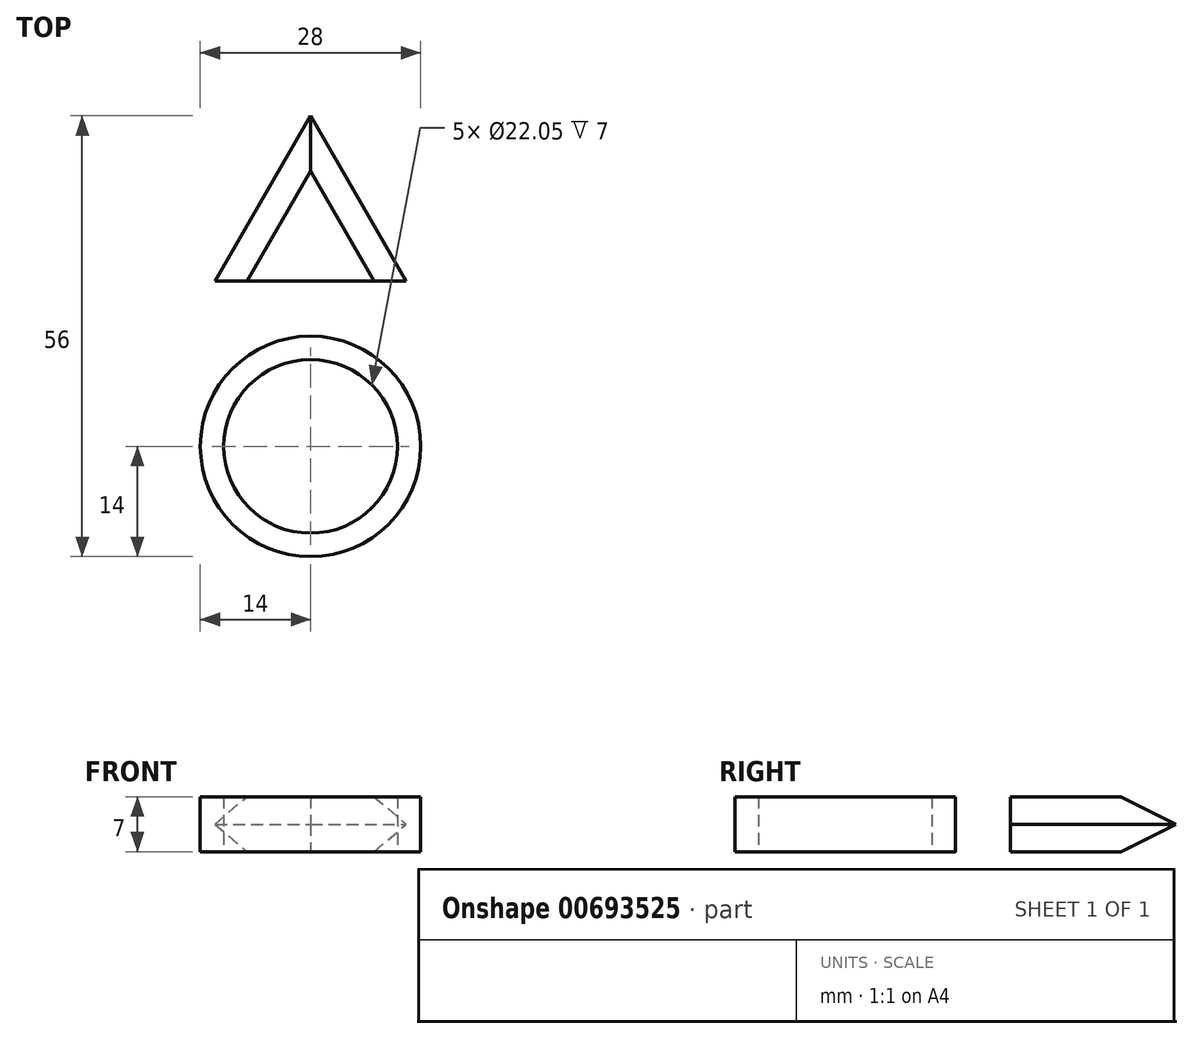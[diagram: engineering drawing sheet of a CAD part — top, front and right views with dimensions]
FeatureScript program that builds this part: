
annotation { "Feature Type Name" : "Feature", "Feature Type Description" : "" }
export const myFeature = defineFeature(function(context is Context, id is Id, definition is map)
    precondition{}
    {
        {
            var Q0;
            Q0=qCreatedBy(makeId("Top.planeOp"),FACE);
            var sketch = newSketch(context, id + "F0", { "sketchPlane" : qUnion([Q0])});
            skCircle(sketch, "E0.cCircle", {"center": v(0, 18.9) * mm, "radius": 14 * mm, "construction": true});
            skLineSegment(sketch, "E0.0", {"start": v(12.12, 11.9) * mm, "end": v(-12.12, 11.9) * mm});
            skLineSegment(sketch, "E0.1", {"start": v(-12.12, 11.9) * mm, "end": v(0, 32.9) * mm});
            skLineSegment(sketch, "E0.2", {"start": v(0, 32.9) * mm, "end": v(12.12, 11.9) * mm});
            skCircle(sketch, "E1.cCircle", {"center": v(0, 4.9) * mm, "radius": 14 * mm, "construction": true});
            skPoint(sketch, "E1.cCircle.centerSnap0", {"position": v(0, 11.9) * mm});
            skLineSegment(sketch, "E1.0", {"start": v(0, -9.1) * mm, "end": v(-12.12, 11.9) * mm});
            skLineSegment(sketch, "E1.1", {"start": v(-12.12, 11.9) * mm, "end": v(12.12, 11.9) * mm});
            skLineSegment(sketch, "E1.2", {"start": v(12.12, 11.9) * mm, "end": v(0, -9.1) * mm});
            skCircle(sketch, "E2", {"center": v(0, -9.1) * mm, "radius": 14 * mm});
            skCircle(sketch, "E3", {"center": v(0, -9.1) * mm, "radius": 11.03 * mm});
            skSolve(sketch);
        }
        {
            var Q0;
            Q0=makeQuery(id+"F0.imprint","IMPRINT",FACE,{"disambiguationData":[TD([[makeQuery(id+"F0.imprint","IMPRINT",EDGE,{"derivedFrom":sQuery(id+"F0.wireOp",EDGE,"E0.1")}),-1.0]])]});
            var Q1;
            {var subQ0=sQuery(id+"F0.wireOp",EDGE,"E1.1");Q1=makeQuery(id+"F0.imprint","IMPRINT",FACE,{"disambiguationData":[TD([[makeQuery(id+"F0.imprint","IMPRINT",EDGE,{"derivedFrom":subQ0}),-1.0]])]});}
            var Q2;
            {var subQ0=sQuery(id+"F0.wireOp",EDGE,"E2");var subQ1=sQuery(id+"F0.wireOp",EDGE,"E1.0");var subQ2=makeQuery(id+"F0.imprint","INTERSECT",VERTEX,{"derivedFrom":[subQ1,subQ0]});Q2=makeQuery(id+"F0.imprint","IMPRINT",FACE,{"disambiguationData":[TD([[makeQuery(id+"F0.imprint","IMPRINT",EDGE,{"disambiguationData":[TD([[subQ2,1.0]])],"derivedFrom":subQ1}),-1.0]])]});}
            var Q3;
            {var subQ0=sQuery(id+"F0.wireOp",EDGE,"E2");var subQ1=sQuery(id+"F0.wireOp",EDGE,"E1.0");var subQ2=makeQuery(id+"F0.imprint","INTERSECT",VERTEX,{"derivedFrom":[subQ1,subQ0]});Q3=makeQuery(id+"F0.imprint","IMPRINT",FACE,{"disambiguationData":[TD([[makeQuery(id+"F0.imprint","IMPRINT",EDGE,{"disambiguationData":[TD([[subQ2,1.0]])],"derivedFrom":subQ1}),1.0]])]});}
            extrude(context, id + "F1", {"entities" : qUnion([Q0, Q1, Q2, Q3]), "depth" : 7 * mm, "offsetDistance" : 25.4 * mm});
        }
        {
            var Q0;
            Q0=makeQuery(id+"F1.opExtrude","SWEPT_BODY",BODY,{"disambiguationData":[OSD([sQuery(id+"F0.wireOp",EDGE,"E0.1"),sQuery(id+"F0.wireOp",EDGE,"E0.2"),sQuery(id+"F0.wireOp",EDGE,"E1.0"),sQuery(id+"F0.wireOp",EDGE,"E1.2"),sQuery(id+"F0.wireOp",EDGE,"E2"),sQuery(id+"F0.wireOp",EDGE,"E3")])]});
            var Q1;
            Q1=makeQuery(id+"F1.opExtrude","SWEPT_FACE",FACE,{"disambiguationData":[OSD([sQuery(id+"F0.wireOp",EDGE,"E2")])]});
            circularPattern(context, id + "F2", {"operationType" : NewBodyOperationType.ADD, "entities" : qUnion([Q0]), "axis" : qUnion([Q1]), "angle" : 360 * degree, "instanceCount" : 5, "equalSpace" : true});
        }
        {
            var Q0;
            Q0=makeQuery(id+"F2.opPattern","COPY",EDGE,{"derivedFrom":makeQuery(id+"F1.opExtrude","CAP_EDGE",EDGE,{"disambiguationData":[OSD([sQuery(id+"F0.wireOp",EDGE,"E0.1")])],"isStart":false}),"instanceName":"3"});
            var Q1;
            Q1=makeQuery(id+"F2.opPattern","COPY",EDGE,{"derivedFrom":makeQuery(id+"F1.opExtrude","CAP_EDGE",EDGE,{"disambiguationData":[OSD([sQuery(id+"F0.wireOp",EDGE,"E0.2")])],"isStart":false}),"instanceName":"3"});
            var Q2;
            Q2=makeQuery(id+"F2.opPattern","COPY",EDGE,{"derivedFrom":makeQuery(id+"F1.opExtrude","CAP_EDGE",EDGE,{"disambiguationData":[OSD([sQuery(id+"F0.wireOp",EDGE,"E1.0")])],"isStart":false}),"instanceName":"4"});
            var Q3;
            Q3=makeQuery(id+"F2.opPattern","COPY",EDGE,{"derivedFrom":makeQuery(id+"F1.opExtrude","CAP_EDGE",EDGE,{"disambiguationData":[OSD([sQuery(id+"F0.wireOp",EDGE,"E1.2")])],"isStart":false}),"instanceName":"3"});
            var Q4;
            Q4=makeQuery(id+"F2.opPattern","COPY",EDGE,{"derivedFrom":makeQuery(id+"F1.opExtrude","CAP_EDGE",EDGE,{"disambiguationData":[OSD([sQuery(id+"F0.wireOp",EDGE,"E0.1")])],"isStart":false}),"instanceName":"4"});
            var Q5;
            Q5=makeQuery(id+"F2.opPattern","COPY",EDGE,{"derivedFrom":makeQuery(id+"F1.opExtrude","CAP_EDGE",EDGE,{"disambiguationData":[OSD([sQuery(id+"F0.wireOp",EDGE,"E0.2")])],"isStart":false}),"instanceName":"4"});
            var Q6;
            Q6=makeQuery(id+"F1.opExtrude","CAP_EDGE",EDGE,{"disambiguationData":[OSD([sQuery(id+"F0.wireOp",EDGE,"E1.0")])],"isStart":false});
            var Q7;
            Q7=makeQuery(id+"F2.opPattern","COPY",EDGE,{"derivedFrom":makeQuery(id+"F1.opExtrude","CAP_EDGE",EDGE,{"disambiguationData":[OSD([sQuery(id+"F0.wireOp",EDGE,"E1.2")])],"isStart":false}),"instanceName":"4"});
            var Q8;
            Q8=makeQuery(id+"F1.opExtrude","CAP_EDGE",EDGE,{"disambiguationData":[OSD([sQuery(id+"F0.wireOp",EDGE,"E0.1")])],"isStart":false});
            var Q9;
            Q9=makeQuery(id+"F1.opExtrude","CAP_EDGE",EDGE,{"disambiguationData":[OSD([sQuery(id+"F0.wireOp",EDGE,"E0.2")])],"isStart":false});
            var Q10;
            Q10=makeQuery(id+"F1.opExtrude","CAP_EDGE",EDGE,{"disambiguationData":[OSD([sQuery(id+"F0.wireOp",EDGE,"E1.2")])],"isStart":false});
            var Q11;
            Q11=makeQuery(id+"F2.opPattern","COPY",EDGE,{"derivedFrom":makeQuery(id+"F1.opExtrude","CAP_EDGE",EDGE,{"disambiguationData":[OSD([sQuery(id+"F0.wireOp",EDGE,"E1.0")])],"isStart":false}),"instanceName":"1"});
            var Q12;
            Q12=makeQuery(id+"F2.opPattern","COPY",EDGE,{"derivedFrom":makeQuery(id+"F1.opExtrude","CAP_EDGE",EDGE,{"disambiguationData":[OSD([sQuery(id+"F0.wireOp",EDGE,"E0.1")])],"isStart":false}),"instanceName":"1"});
            var Q13;
            Q13=makeQuery(id+"F2.opPattern","COPY",EDGE,{"derivedFrom":makeQuery(id+"F1.opExtrude","CAP_EDGE",EDGE,{"disambiguationData":[OSD([sQuery(id+"F0.wireOp",EDGE,"E0.2")])],"isStart":false}),"instanceName":"1"});
            var Q14;
            Q14=makeQuery(id+"F2.opPattern","COPY",EDGE,{"derivedFrom":makeQuery(id+"F1.opExtrude","CAP_EDGE",EDGE,{"disambiguationData":[OSD([sQuery(id+"F0.wireOp",EDGE,"E1.2")])],"isStart":false}),"instanceName":"1"});
            var Q15;
            Q15=makeQuery(id+"F2.opPattern","COPY",EDGE,{"derivedFrom":makeQuery(id+"F1.opExtrude","CAP_EDGE",EDGE,{"disambiguationData":[OSD([sQuery(id+"F0.wireOp",EDGE,"E1.0")])],"isStart":false}),"instanceName":"2"});
            var Q16;
            Q16=makeQuery(id+"F2.opPattern","COPY",EDGE,{"derivedFrom":makeQuery(id+"F1.opExtrude","CAP_EDGE",EDGE,{"disambiguationData":[OSD([sQuery(id+"F0.wireOp",EDGE,"E0.1")])],"isStart":false}),"instanceName":"2"});
            var Q17;
            Q17=makeQuery(id+"F2.opPattern","COPY",EDGE,{"derivedFrom":makeQuery(id+"F1.opExtrude","CAP_EDGE",EDGE,{"disambiguationData":[OSD([sQuery(id+"F0.wireOp",EDGE,"E0.2")])],"isStart":false}),"instanceName":"2"});
            var Q18;
            Q18=makeQuery(id+"F2.opPattern","COPY",EDGE,{"derivedFrom":makeQuery(id+"F1.opExtrude","CAP_EDGE",EDGE,{"disambiguationData":[OSD([sQuery(id+"F0.wireOp",EDGE,"E1.2")])],"isStart":false}),"instanceName":"2"});
            var Q19;
            Q19=makeQuery(id+"F2.opPattern","COPY",EDGE,{"derivedFrom":makeQuery(id+"F1.opExtrude","CAP_EDGE",EDGE,{"disambiguationData":[OSD([sQuery(id+"F0.wireOp",EDGE,"E1.0")])],"isStart":false}),"instanceName":"3"});
            var Q20;
            Q20=makeQuery(id+"F2.opPattern","COPY",EDGE,{"derivedFrom":makeQuery(id+"F1.opExtrude","CAP_EDGE",EDGE,{"disambiguationData":[OSD([sQuery(id+"F0.wireOp",EDGE,"E0.1")])],"isStart":true}),"instanceName":"3"});
            var Q21;
            Q21=makeQuery(id+"F2.opPattern","COPY",EDGE,{"derivedFrom":makeQuery(id+"F1.opExtrude","CAP_EDGE",EDGE,{"disambiguationData":[OSD([sQuery(id+"F0.wireOp",EDGE,"E0.2")])],"isStart":true}),"instanceName":"3"});
            var Q22;
            Q22=makeQuery(id+"F2.opPattern","COPY",EDGE,{"derivedFrom":makeQuery(id+"F1.opExtrude","CAP_EDGE",EDGE,{"disambiguationData":[OSD([sQuery(id+"F0.wireOp",EDGE,"E1.0")])],"isStart":true}),"instanceName":"3"});
            var Q23;
            Q23=makeQuery(id+"F2.opPattern","COPY",EDGE,{"derivedFrom":makeQuery(id+"F1.opExtrude","CAP_EDGE",EDGE,{"disambiguationData":[OSD([sQuery(id+"F0.wireOp",EDGE,"E1.2")])],"isStart":true}),"instanceName":"2"});
            var Q24;
            Q24=makeQuery(id+"F2.opPattern","COPY",EDGE,{"derivedFrom":makeQuery(id+"F1.opExtrude","CAP_EDGE",EDGE,{"disambiguationData":[OSD([sQuery(id+"F0.wireOp",EDGE,"E0.2")])],"isStart":true}),"instanceName":"2"});
            var Q25;
            Q25=makeQuery(id+"F2.opPattern","COPY",EDGE,{"derivedFrom":makeQuery(id+"F1.opExtrude","CAP_EDGE",EDGE,{"disambiguationData":[OSD([sQuery(id+"F0.wireOp",EDGE,"E0.1")])],"isStart":true}),"instanceName":"2"});
            var Q26;
            Q26=makeQuery(id+"F2.opPattern","COPY",EDGE,{"derivedFrom":makeQuery(id+"F1.opExtrude","CAP_EDGE",EDGE,{"disambiguationData":[OSD([sQuery(id+"F0.wireOp",EDGE,"E1.0")])],"isStart":true}),"instanceName":"2"});
            var Q27;
            Q27=makeQuery(id+"F2.opPattern","COPY",EDGE,{"derivedFrom":makeQuery(id+"F1.opExtrude","CAP_EDGE",EDGE,{"disambiguationData":[OSD([sQuery(id+"F0.wireOp",EDGE,"E1.2")])],"isStart":true}),"instanceName":"1"});
            var Q28;
            Q28=makeQuery(id+"F2.opPattern","COPY",EDGE,{"derivedFrom":makeQuery(id+"F1.opExtrude","CAP_EDGE",EDGE,{"disambiguationData":[OSD([sQuery(id+"F0.wireOp",EDGE,"E0.2")])],"isStart":true}),"instanceName":"1"});
            var Q29;
            Q29=makeQuery(id+"F2.opPattern","COPY",EDGE,{"derivedFrom":makeQuery(id+"F1.opExtrude","CAP_EDGE",EDGE,{"disambiguationData":[OSD([sQuery(id+"F0.wireOp",EDGE,"E0.1")])],"isStart":true}),"instanceName":"1"});
            var Q30;
            Q30=makeQuery(id+"F2.opPattern","COPY",EDGE,{"derivedFrom":makeQuery(id+"F1.opExtrude","CAP_EDGE",EDGE,{"disambiguationData":[OSD([sQuery(id+"F0.wireOp",EDGE,"E1.0")])],"isStart":true}),"instanceName":"1"});
            var Q31;
            Q31=makeQuery(id+"F1.opExtrude","CAP_EDGE",EDGE,{"disambiguationData":[OSD([sQuery(id+"F0.wireOp",EDGE,"E1.2")])],"isStart":true});
            var Q32;
            Q32=makeQuery(id+"F1.opExtrude","CAP_EDGE",EDGE,{"disambiguationData":[OSD([sQuery(id+"F0.wireOp",EDGE,"E0.2")])],"isStart":true});
            var Q33;
            Q33=makeQuery(id+"F1.opExtrude","CAP_EDGE",EDGE,{"disambiguationData":[OSD([sQuery(id+"F0.wireOp",EDGE,"E0.1")])],"isStart":true});
            var Q34;
            Q34=makeQuery(id+"F1.opExtrude","CAP_EDGE",EDGE,{"disambiguationData":[OSD([sQuery(id+"F0.wireOp",EDGE,"E1.0")])],"isStart":true});
            var Q35;
            Q35=makeQuery(id+"F2.opPattern","COPY",EDGE,{"derivedFrom":makeQuery(id+"F1.opExtrude","CAP_EDGE",EDGE,{"disambiguationData":[OSD([sQuery(id+"F0.wireOp",EDGE,"E1.2")])],"isStart":true}),"instanceName":"4"});
            var Q36;
            Q36=makeQuery(id+"F2.opPattern","COPY",EDGE,{"derivedFrom":makeQuery(id+"F1.opExtrude","CAP_EDGE",EDGE,{"disambiguationData":[OSD([sQuery(id+"F0.wireOp",EDGE,"E0.2")])],"isStart":true}),"instanceName":"4"});
            var Q37;
            Q37=makeQuery(id+"F2.opPattern","COPY",EDGE,{"derivedFrom":makeQuery(id+"F1.opExtrude","CAP_EDGE",EDGE,{"disambiguationData":[OSD([sQuery(id+"F0.wireOp",EDGE,"E0.1")])],"isStart":true}),"instanceName":"4"});
            var Q38;
            Q38=makeQuery(id+"F2.opPattern","COPY",EDGE,{"derivedFrom":makeQuery(id+"F1.opExtrude","CAP_EDGE",EDGE,{"disambiguationData":[OSD([sQuery(id+"F0.wireOp",EDGE,"E1.0")])],"isStart":true}),"instanceName":"4"});
            var Q39;
            Q39=makeQuery(id+"F2.opPattern","COPY",EDGE,{"derivedFrom":makeQuery(id+"F1.opExtrude","CAP_EDGE",EDGE,{"disambiguationData":[OSD([sQuery(id+"F0.wireOp",EDGE,"E1.2")])],"isStart":true}),"instanceName":"3"});
            chamfer(context, id + "F3", {"entities" : qUnion([Q0, Q1, Q2, Q3, Q4, Q5, Q6, Q7, Q8, Q9, Q10, Q11, Q12, Q13, Q14, Q15, Q16, Q17, Q18, Q19, Q20, Q21, Q22, Q23, Q24, Q25, Q26, Q27, Q28, Q29, Q30, Q31, Q32, Q33, Q34, Q35, Q36, Q37, Q38, Q39]), "width" : 3.5 * mm, "tangentPropagation" : true});
        }
    });
